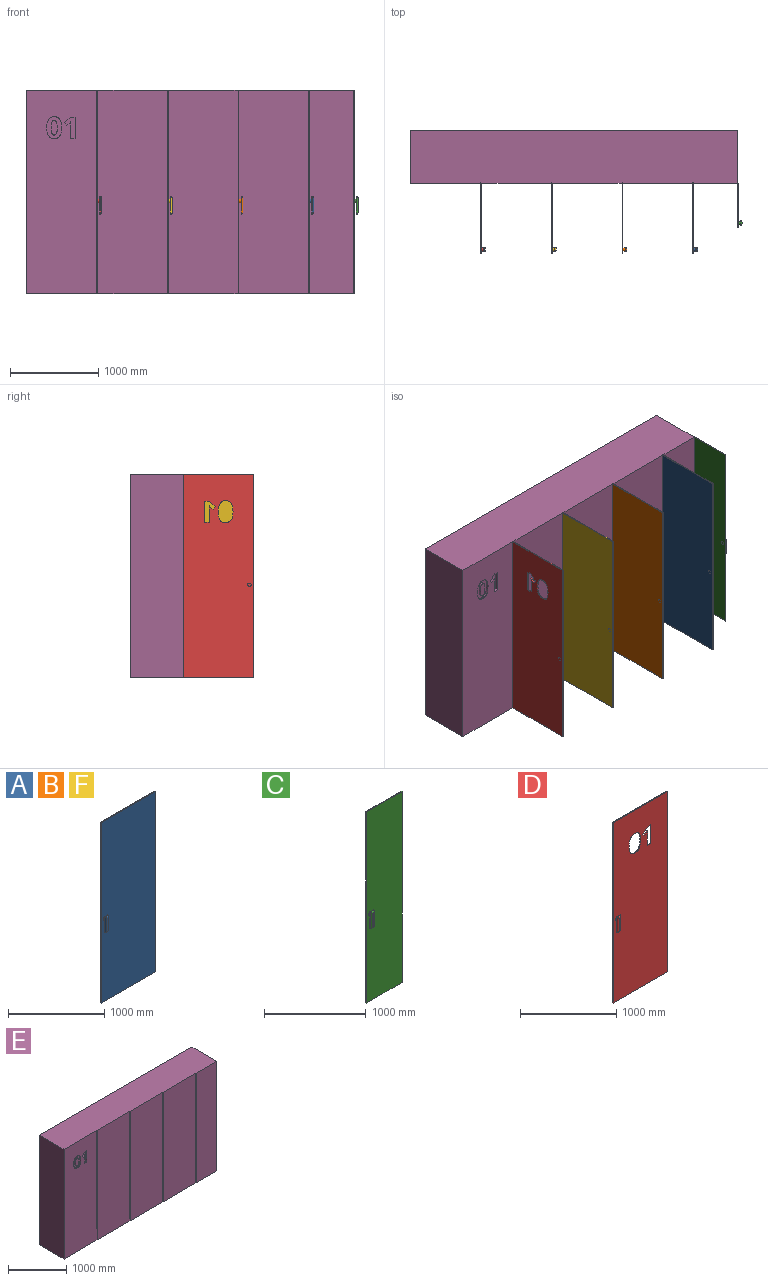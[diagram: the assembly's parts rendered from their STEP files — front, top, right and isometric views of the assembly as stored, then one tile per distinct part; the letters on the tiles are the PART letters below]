
ASSEMBLY  parts=6 mates=5
PART A: 17 faces, bbox 796x55x2300 mm
  f0: cylinder r=20mm len=40mm, axis (0,1,0), area 3141.6mm2, adj f6,f15
  f1: plane 50x5mm, normal (0,0,-1), area 250mm2, adj f2,f4,f6,f7
  f2: plane 200x5mm, normal (1,0,0), area 1000mm2, adj f1,f3,f6,f8
  f3: plane 50x5mm, normal (0,0,1), area 250mm2, adj f2,f4,f6,f10
  f4: plane 200x5mm, normal (-1,0,0), area 1000mm2, adj f1,f3,f6,f9
  f5: plane 170x20mm, normal (0,-1,0), area 3400mm2, adj f7,f8,f9,f10
  f6: plane 200x50mm, normal (0,1,0), area 8743.4mm2, adj f0,f1,f2,f3,f4
  f7: cylinder r=15mm len=50mm, axis (-1,0,0), area 921.2mm2, adj f1,f5,f8,f9
  f8: cylinder r=15mm len=200mm, axis (0,0,-1), area 4455.5mm2, adj f2,f5,f7,f10
  f9: cylinder r=15mm len=200mm, axis (0,0,1), area 4455.5mm2, adj f4,f5,f7,f10
  f10: cylinder r=15mm len=50mm, axis (1,0,0), area 921.2mm2, adj f3,f5,f8,f9
  f11: plane 796x10mm, normal (0,0,1), area 7960mm2, adj f12,f14,f15,f16
  f12: plane 2300x10mm, normal (-1,0,0), area 23000mm2, adj f11,f13,f15,f16
  f13: plane 796x10mm, normal (0,0,-1), area 7960mm2, adj f12,f14,f15,f16
  f14: plane 2300x10mm, normal (1,0,0), area 23000mm2, adj f11,f13,f15,f16
  f15: plane 2300x796mm, normal (0,-1,0), area 1829543.4mm2, adj f0,f11,f12,f13,f14
  f16: plane 2300x796mm, normal (0,1,0), area 1830800mm2, adj f11,f12,f13,f14
PART B: same geometry as A
PART C: 17 faces, bbox 498x55x2300 mm
  f0: plane 498x10mm, normal (0,0,1), area 4980mm2, adj f1,f3,f4,f5
  f1: plane 2300x10mm, normal (-1,0,0), area 23000mm2, adj f0,f2,f4,f5
  f2: plane 498x10mm, normal (0,0,-1), area 4980mm2, adj f1,f3,f4,f5
  f3: plane 2300x10mm, normal (1,0,0), area 23000mm2, adj f0,f2,f4,f5
  f4: plane 2300x498mm, normal (0,-1,0), area 1144143.4mm2, adj f0,f1,f2,f3,f6
  f5: plane 2300x498mm, normal (0,1,0), area 1145400mm2, adj f0,f1,f2,f3
  f6: cylinder r=20mm len=40mm, axis (0,1,0), area 3141.6mm2, adj f4,f12
  f7: plane 50x5mm, normal (0,0,-1), area 250mm2, adj f8,f10,f12,f13
  f8: plane 200x5mm, normal (1,0,0), area 1000mm2, adj f7,f9,f12,f14
  f9: plane 50x5mm, normal (0,0,1), area 250mm2, adj f8,f10,f12,f16
  f10: plane 200x5mm, normal (-1,0,0), area 1000mm2, adj f7,f9,f12,f15
  f11: plane 170x20mm, normal (0,-1,0), area 3400mm2, adj f13,f14,f15,f16
  f12: plane 200x50mm, normal (0,1,0), area 8743.4mm2, adj f6,f7,f8,f9,f10
  f13: cylinder r=15mm len=50mm, axis (-1,0,0), area 921.2mm2, adj f7,f11,f14,f15
  f14: cylinder r=15mm len=200mm, axis (0,0,-1), area 4455.5mm2, adj f8,f11,f13,f16
  f15: cylinder r=15mm len=200mm, axis (0,0,1), area 4455.5mm2, adj f10,f11,f13,f16
  f16: cylinder r=15mm len=50mm, axis (1,0,0), area 921.2mm2, adj f9,f11,f14,f15
PART D: 35 faces, bbox 798x55x2300 mm
  f0: cylinder r=20mm len=40mm, axis (0,1,0), area 3141.6mm2, adj f6,f33
  f1: plane 200x5mm, normal (1,0,0), area 1000mm2, adj f2,f4,f6,f7
  f2: plane 50x5mm, normal (0,0,1), area 250mm2, adj f1,f3,f6,f8
  f3: plane 200x5mm, normal (-1,0,0), area 1000mm2, adj f2,f4,f6,f10
  f4: plane 50x5mm, normal (0,0,-1), area 250mm2, adj f1,f3,f6,f9
  f5: plane 170x20mm, normal (0,-1,0), area 3400mm2, adj f7,f8,f9,f10
  f6: plane 200x50mm, normal (0,1,0), area 8743.4mm2, adj f0,f1,f2,f3,f4
  f7: cylinder r=15mm len=200mm, axis (0,0,-1), area 4455.5mm2, adj f1,f5,f8,f9
  f8: cylinder r=15mm len=50mm, axis (1,0,0), area 921.2mm2, adj f2,f5,f7,f10
  f9: cylinder r=15mm len=50mm, axis (-1,0,0), area 921.2mm2, adj f4,f5,f7,f10
  f10: cylinder r=15mm len=200mm, axis (0,0,1), area 4455.5mm2, adj f3,f5,f8,f9
  f11: plane 241.59x10mm, normal (-1,0,0), area 2415.9mm2, adj f12,f32,f33,f34
  f12: plane 51.08x10mm, normal (0,0,1), area 510.8mm2, adj f11,f13,f33,f34
  f13: plane 139.8x10mm, normal (1,0,0), area 1398mm2, adj f12,f14,f33,f34
  f14: plane 22.95x10mm, normal (1,0,-0.02), area 229.5mm2, adj f13,f15,f33,f34
  f15: plane 25.12x10mm, normal (1,0,-0.03), area 251.3mm2, adj f14,f16,f33,f34
  f16: extruded ~17.66x16.66mm, area 242.8mm2, adj f15,f17,f33,f34
  f17: plane 27.76x22.31mm, normal (-0.63,0,0.78), area 356.2mm2, adj f16,f18,f33,f34
  f18: plane 30.72x24.64mm, normal (0.78,0,0.63), area 393.8mm2, adj f17,f19,f33,f34
  f19: plane 77.83x61.97mm, normal (0.62,0,-0.78), area 994.9mm2, adj f18,f32,f33,f34
  f20: extruded ~92.9x21.39mm, area 966.8mm2, adj f21,f30,f33,f34
  f21: extruded ~93.67x20.73mm, area 972.8mm2, adj f20,f22,f33,f34
  f22: extruded ~63.87x30.43mm, area 738.9mm2, adj f21,f23,f33,f34
  f23: extruded ~63.05x31.41mm, area 736.2mm2, adj f22,f24,f33,f34
  f24: extruded ~92.69x21.23mm, area 964.4mm2, adj f23,f25,f33,f34
  f25: extruded ~94.3x20.67mm, area 978.9mm2, adj f24,f26,f33,f34
  f26: extruded ~63.61x30.32mm, area 735.9mm2, adj f25,f30,f33,f34
  f27: plane 2300x10mm, normal (1,0,0), area 23000mm2, adj f28,f31,f33,f34
  f28: plane 798x10mm, normal (0,0,1), area 7980mm2, adj f27,f29,f33,f34
  f29: plane 2300x10mm, normal (-1,0,0), area 23000mm2, adj f28,f31,f33,f34
  f30: extruded ~63.21x31.73mm, area 739.2mm2, adj f20,f26,f33,f34
  f31: plane 798x10mm, normal (0,0,-1), area 7980mm2, adj f27,f29,f33,f34
  f32: plane 41.98x10mm, normal (0,0,-1), area 419.8mm2, adj f11,f19,f33,f34
  f33: plane 2300x798mm, normal (0,-1,0), area 1783995.4mm2, adj f0,f11,f12,f13,f14,f15,f16,f17
  f34: plane 2300x798mm, normal (0,1,0), area 1785252mm2, adj f11,f12,f13,f14,f15,f16,f17,f18
PART E: 51 faces, bbox 3700x600x2300 mm
  f0: plane 2300x798mm, normal (0,-1,0), area 1785252mm2, adj f1,f2,f7,f21,f29,f30,f31,f32
  f1: plane 3700x600mm, normal (0,0,-1), area 2219968mm2, adj f0,f3,f4,f5,f6,f7,f8,f9
  f2: plane 3700x600mm, normal (0,0,1), area 2219968mm2, adj f0,f3,f4,f5,f6,f7,f8,f9
  f3: plane 2300x796mm, normal (0,-1,0), area 1830800mm2, adj f1,f2,f18,f20
  f4: plane 2300x796mm, normal (0,-1,0), area 1830800mm2, adj f1,f2,f15,f17
  f5: plane 2300x796mm, normal (0,-1,0), area 1830800mm2, adj f1,f2,f12,f14
  f6: plane 2300x498mm, normal (0,-1,0), area 1145400mm2, adj f1,f2,f8,f11
  f7: plane 2300x600mm, normal (-1,0,0), area 1380000mm2, adj f0,f1,f2,f9
  f8: plane 2300x600mm, normal (1,0,0), area 1380000mm2, adj f1,f2,f6,f9
  f9: plane 3700x2300mm, normal (0,1,0), area 8510000mm2, adj f1,f2,f7,f8
  f10: plane 2300x4mm, normal (0,-1,0), area 9200mm2, adj f1,f2,f11,f12
  f11: plane 2300x2mm, normal (-1,0,0), area 4600mm2, adj f1,f2,f6,f10
  f12: plane 2300x2mm, normal (1,0,0), area 4600mm2, adj f1,f2,f5,f10
  f13: plane 2300x4mm, normal (0,-1,0), area 9200mm2, adj f1,f2,f14,f15
  f14: plane 2300x2mm, normal (-1,0,0), area 4600mm2, adj f1,f2,f5,f13
  f15: plane 2300x2mm, normal (1,0,0), area 4600mm2, adj f1,f2,f4,f13
  f16: plane 2300x4mm, normal (0,-1,0), area 9200mm2, adj f1,f2,f17,f18
  f17: plane 2300x2mm, normal (-1,0,0), area 4600mm2, adj f1,f2,f4,f16
  f18: plane 2300x2mm, normal (1,0,0), area 4600mm2, adj f1,f2,f3,f16
  f19: plane 2300x4mm, normal (0,-1,0), area 9200mm2, adj f1,f2,f20,f21
  f20: plane 2300x2mm, normal (-1,0,0), area 4600mm2, adj f1,f2,f3,f19
  f21: plane 2300x2mm, normal (1,0,0), area 4600mm2, adj f0,f1,f2,f19
  f22: extruded ~63.66x25mm, area 1611mm2, adj f23,f37,f38,f50
  f23: extruded ~63.87x25mm, area 1616.6mm2, adj f22,f24,f38,f50
  f24: extruded ~25.78x25mm, area 864.1mm2, adj f23,f25,f38,f50
  f25: extruded ~25.7x25mm, area 860.7mm2, adj f24,f26,f38,f50
  f26: extruded ~63.87x25mm, area 1618.1mm2, adj f25,f27,f38,f50
  f27: extruded ~63.43x25mm, area 1606.3mm2, adj f26,f28,f38,f50
  f28: extruded ~25.8x25mm, area 865mm2, adj f27,f37,f38,f50
  f29: extruded ~93.67x25mm, area 2432mm2, adj f0,f30,f36,f38
  f30: extruded ~92.9x25mm, area 2417.1mm2, adj f0,f29,f31,f38
  f31: extruded ~63.21x31.73mm, area 1848.1mm2, adj f0,f30,f32,f38
  f32: extruded ~63.61x30.32mm, area 1839.8mm2, adj f0,f31,f33,f38
  f33: extruded ~94.3x25mm, area 2447.3mm2, adj f0,f32,f34,f38
  f34: extruded ~92.69x25mm, area 2410.9mm2, adj f0,f33,f35,f38
  f35: extruded ~63.05x31.41mm, area 1840.4mm2, adj f0,f34,f36,f38
  f36: extruded ~63.87x30.43mm, area 1847.3mm2, adj f0,f29,f35,f38
  f37: extruded ~25.86x25mm, area 863.4mm2, adj f22,f28,f38,f50
  f38: plane 248.73x168.89mm, normal (0,-1,0), area 25553.8mm2, adj f22,f23,f24,f25,f26,f27,f28,f29
  f39: plane 51.08x25mm, normal (0,0,1), area 1277mm2, adj f0,f40,f48,f49
  f40: plane 241.59x25mm, normal (-1,0,0), area 6039.8mm2, adj f0,f39,f41,f49
  f41: plane 41.98x25mm, normal (0,0,-1), area 1049.6mm2, adj f0,f40,f42,f49
  f42: plane 77.83x61.97mm, normal (0.62,0,-0.78), area 2487.3mm2, adj f0,f41,f43,f49
  f43: plane 30.72x25mm, normal (0.78,0,0.63), area 984.5mm2, adj f0,f42,f44,f49
  f44: plane 27.76x25mm, normal (-0.63,0,0.78), area 890.4mm2, adj f0,f43,f45,f49
  f45: extruded ~25x17.66mm, area 607.1mm2, adj f0,f44,f46,f49
  f46: plane 25.12x25mm, normal (1,0,-0.03), area 628.2mm2, adj f0,f45,f47,f49
  f47: plane 25x22.95mm, normal (1,0,-0.02), area 573.9mm2, adj f0,f46,f48,f49
  f48: plane 139.8x25mm, normal (1,0,0), area 3495.1mm2, adj f0,f39,f47,f49
  f49: plane 241.59x119.82mm, normal (0,-1,0), area 15097mm2, adj f39,f40,f41,f42,f43,f44,f45,f46
  f50: plane 166.19x67.26mm, normal (0,-1,0), area 9497.2mm2, adj f22,f23,f24,f25,f26,f27,f28,f37
PART F: same geometry as A
PLACE A rot(axis=(0,0,1),90deg) t=(748,-1898,0)mm
PLACE B rot(axis=(0,0,1),90deg) t=(-52,-1898,0)mm
PLACE C rot(axis=(0,0,1),90deg) t=(1250,-4000,0)mm
PLACE D rot(axis=(0,0,1),90deg) t=(-1652,-1098,0)mm
PLACE E t=(-1850,300,0)mm
PLACE F rot(axis=(0,0,1),90deg) t=(-852,-1898,0)mm
MATE revolute E.f2 <-> D.f28  axis (0,0,-1) through (-1052,-300,2300)mm
MATE revolute B.f13 <-> E.f1  axis (0,0,-1) through (548,-300,0)mm
MATE revolute A.f13 <-> E.f1  axis (0,0,-1) through (1348,-300,0)mm
MATE revolute F.f11 <-> E.f2  axis (0,0,-1) through (-252,-300,2300)mm
MATE revolute E.f2 <-> C.f0  axis (0,0,1) through (1850,-300,2300)mm
